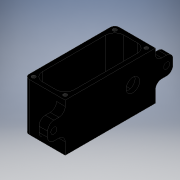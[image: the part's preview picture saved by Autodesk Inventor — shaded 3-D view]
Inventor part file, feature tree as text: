
AUTODESK INVENTOR PART (.ipt)
format: ipt  version: 2019 (Build 230136000, 136)  size: 217,088 bytes
history: native  units: mm
features: other x5, hole x3, fillet x2, extrude x1
ambient origin geometry x8: Origin, YZ Plane, XZ Plane, XY Plane, X Axis, Y Axis, Z Axis, Center Point
bodies: Solid1 (feature_tree), Body (feature_tree)
feature tree (11):
  fillet  "Shell Fillet"  Radius=45.0mm
  hole  "Lid Fastening Holes"  [1 undecoded]
  hole  "Cable Exit Hole"  [1 undecoded]
  extrude  "Flanges"  Depth=50.0mm
  fillet  "Flanges Fillet"  Radius=53.0mm
  hole  "Box Fastening Holes"  [1 undecoded]
  other  "Body Outline"
  other  "Lid Fastening Hole Pattern"
  other  "Cable Exit Hole Position"
  other  "Flanges Outline"
  other  "Box Fastening Hole Pattern"
note: 3 required parameter values undecoded (feature->parameter linkage not recoverable at this tier; creation-order binding heuristic only, values carry confidence <= 0.55)
